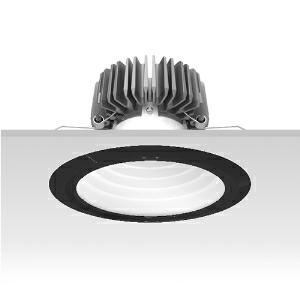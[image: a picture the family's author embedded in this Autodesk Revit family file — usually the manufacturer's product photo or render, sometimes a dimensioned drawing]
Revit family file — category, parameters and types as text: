
# Revit family: 3f_filippi_-_3f_reno_bianco_ampio_3f_filippi_-_30637_a01026_-_3f_reno_200_wh_4000-840_wide___vt_bk_54d8
name_source: partatom
category: Lighting Fixtures
units: mm (PartAtom-declared; Revit-internal decimal feet)

## family parameters
Cut with Voids When Loaded = No
Host = Face
Light Source = No
Part Type = Normal
Room Calculation Point = No
Round Connector Dimension = Use Diameter
Shared = No

## types (1)
- 3F Filippi - 3F Reno Bianco Ampio (1 x LED, 3379 lm, 36 W, 4000 K)
    Apparent Load = 36 VA
    Approval mark = CE
    CIE Flux Codes = 75 94 99 100 100
    Color Rendering = 80
    Color Temperature = 4000 K
    Control Gear = Electronic ballast
    Default Elevation = 1800 mm
    Description = ILLUMINOTECHNICAL
Luminous efficiency 100% (DLOR 100%, ULOR 0%).
Initial luminous flux of the luminaire 3379 lm.
Direct symmetric wide distribution.
Installation Interdistance Transv.D = 1.56 x hu - Long.D = 1.56 x hu.
Tabular UGR (CIE 117 - 4H-8H; S=0.25H; 70/50/20): RUG 22.8 - 22.7.
Beam angle: 74° - 74°.
Luminous efficacy 94 lm/W.
Lifetime (L90/B10): 30000 h. (tq+25°C)
Lifetime (L85/B10): 50000 h. (tq+25°C)
Lifetime (L70/B10): 80000 h. (tq+25°C)
Sudden decreased luminous flux after 50000 hours: 0% (C0).
Photobiological safety in compliance with IEC/TR 62778: RG1 low risk, (IEC 62471).
In compliance with IEC/EN 62722-2-1 - IEC/EN 62717 standards.

SOURCE
Compact LED module 4000/840.
Energy efficiency class (UE 2019/2020 - UE 2019/2015): E.
CIE 13.3 Colour rendering index: CRI >80 (R9 <50%).
IES TM-30 Fidelity Index: Rf = 84 Rg = 95.
CCT nominal colour temperature 4000 K.
Colour initial tolerance (MacAdam): SDCM 3.
Zhaga Book 3 compliant.

MECHANICAL
Passive heat dissipator in die-casting aluminium, oversized, for optimum thermal management of the LED module.
Parabolic element with graduated/concentric rings in white polycarbonate.
Transparent external lens with glossy and satin differentiated surfaces, with a cooling and anti-insect system in methacrylate (PMMA).
Fastening spring clips in stainless steel.
Dimensions: diameter 226 mm, height 146 mm. Weight 1.715 kg.
IP44 protection degree for exposed part, IP20 for recessed part.
Mechanical strength to impacts IK06 (1 joule).
Glow-wire test resistance 650°C.

ELECTRICAL
Wiring on a separate unit.
Halogen Free electronic wiring 230V-50/60Hz, power factor 0.95, THD <25%, constant output current, SELV, class II, 1 driver.
Power of the luminaire 36 W.
ENEC - CE.
SAFE FLICKER: PstLM=<1 and SVM=<0.4 (IEC TR 61547-1 and IEC TR 63158), to ensure a more comfortable and safe light.
Luminaire compliant with EN 60598-2-22 for power supply from a centralised emergency system CPSS (Central Power Supply System), not incorporated in the luminaire - high risk areas excluded. The default power and flux are 100% in AC and 100% in DC.
Ambient temperature from 0°C to +25°C.
Temperature class T6 max 85°C.
Relative humidity UR: <85%.

INSTALLATION
Pull-up recessed fitting.
False ceiling carving: 200 mm.
All accessories dedicated to this product are available on the Catalog and on our website www.3F-Filippi.com.

ACCESSORIES
A01026 - VT transparent glass, tempered, not flammable, locked and in line with the trim, in black polycarbonate.

APPLICATIONS
Environments: architectural, commercial, exhibition areas, transit areas, corridors, shops, display windows, service areas.
In false ceilings with narrow voids.

WARNING
Luminaire designed for disposal/recycling at end-of-life.
Replaceable (LED only) light source by a professional. Replaceable control gear by a professional.
    Height = 0 mm  [stored 0 ft]
    Lamp = 1 x LED
    Lamp Light Flux = 3379 lm
    Lamp Power = 36 W
    Lamp count = 1
    Length = 226 mm
    Lifetime = 50000 h
    Luminous efficacy = 94 lm/W
    Manufacturer = 3F Filippi
    ModVariant = No
    Model = 3F Filippi - 30637+A01026 - 3F Reno 200 WH 4000-840 WIDE + VT BK
    Mounting Place = Ceiling
    Mounting Type = Recessed
    Number of Poles = 1
    OnlyDefault = Yes
    Power Factor = 1
    Product Name = 3F Filippi - 3F Reno Bianco Ampio
    Product group = recessed luminaire
    ProductGroupID = 4
    Protection Class = Protection class II
    Protection Degree = IP 20
    RLX_Detail_Level = 1
    RLX_Emergency_Light_Flux = 0 lm
    RLX_Emergency_Type = 0
    RLX_Emergency_Type_DB = No
    RlxData = <blob elided: 100333 chars, md5=7739b927>
    Socket = socket
    Standby Power = 0 W
    System Light Flux = 3379 lm
    System Power = 36 W
    Type Comments = Product without accessories
    Type Image = 3ffilippi_3f_reno_200_wh__a01026.jpg
    URL = http://relux.com
    VarID = ---
    Voltage = 0 V
    Weight = 0.00 kg
    Width = 0 mm  [stored 0 ft]

note: [stored X ft] marks values corroborated as IEEE doubles in the binary element streams (Revit-internal decimal feet)

## geometry (parser evidence)
native form markers: Blend x4, Sweep x10
no freeform markers — native parametric forms only
